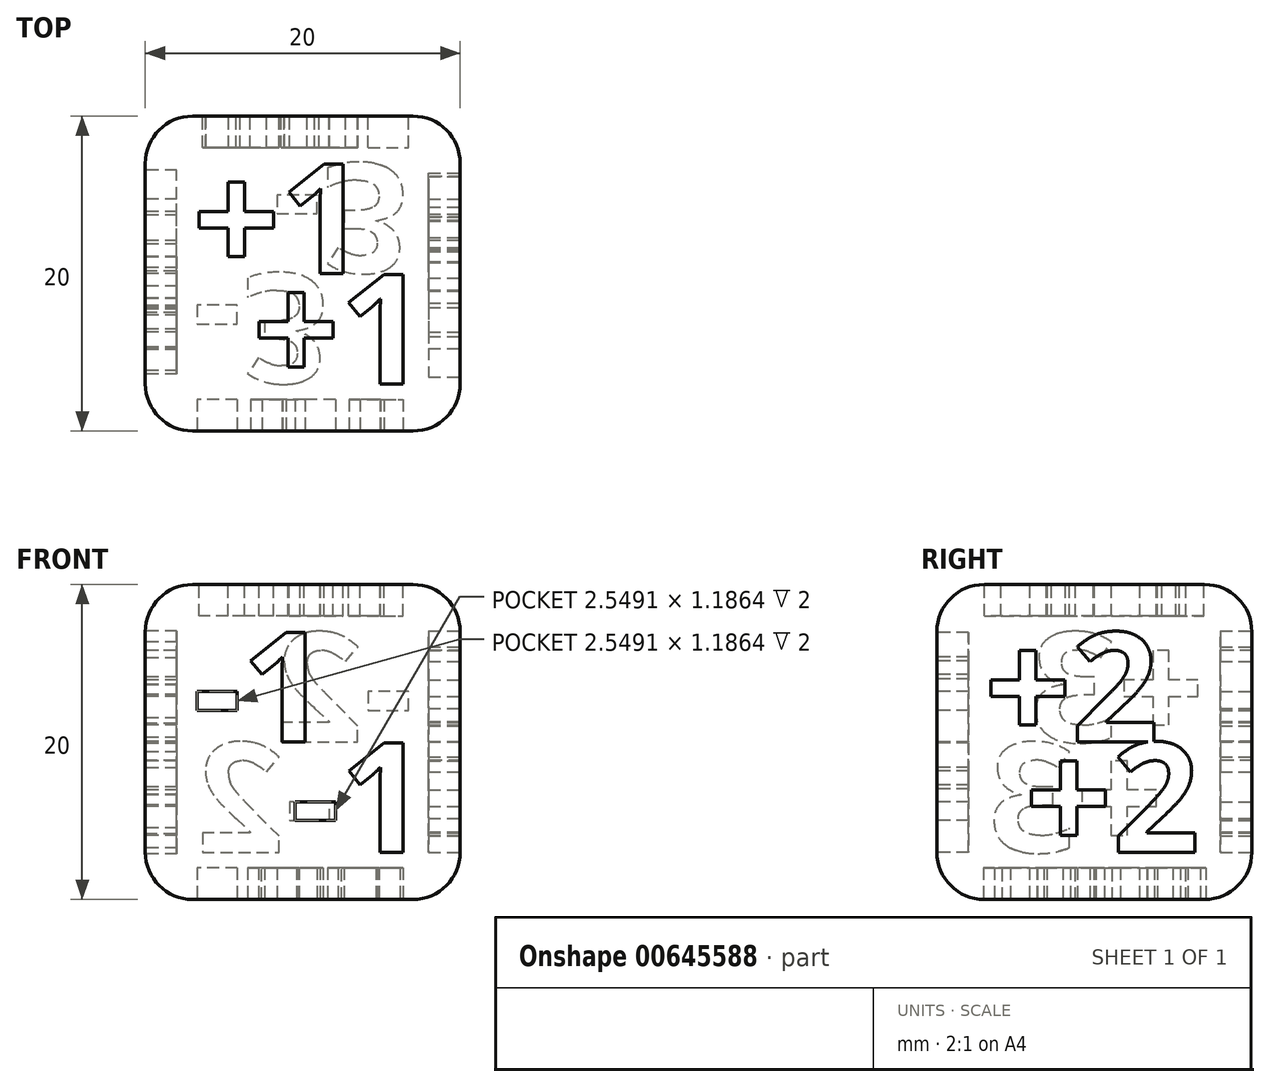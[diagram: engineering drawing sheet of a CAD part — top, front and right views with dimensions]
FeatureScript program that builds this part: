
annotation { "Feature Type Name" : "Feature", "Feature Type Description" : "" }
export const myFeature = defineFeature(function(context is Context, id is Id, definition is map)
    precondition{}
    {
        {
            var Q0;
            Q0=qCreatedBy(makeId("Top.planeOp"),FACE);
            var sketch = newSketch(context, id + "F0", { "sketchPlane" : qUnion([Q0])});
            skLineSegment(sketch, "E0.bottom", {"start": v(0, 0) * mm, "end": v(20, 0) * mm});
            skLineSegment(sketch, "E0.top", {"start": v(0, 20) * mm, "end": v(20, 20) * mm});
            skLineSegment(sketch, "E0.left", {"start": v(0, 0) * mm, "end": v(0, 20) * mm});
            skLineSegment(sketch, "E0.right", {"start": v(20, 0) * mm, "end": v(20, 20) * mm});
            skSolve(sketch);
        }
        {
            var Q0;
            Q0 = qSketchRegion(id + "F0", true);
            extrude(context, id + "F1", {"entities" : qUnion([Q0]), "depth" : 20 * mm, "offsetDistance" : 25 * mm});
        }
        {
            var Q0;
            Q0=makeQuery(id+"F1.opExtrude","CAP_EDGE",EDGE,{"disambiguationData":[OSD([sQuery(id+"F0.wireOp",EDGE,"E0.top")])],"isStart":true});
            var Q1;
            Q1=makeQuery(id+"F1.opExtrude","SWEPT_EDGE",EDGE,{"disambiguationData":[OSD([sQuery(id+"F0.wireOp",EDGE,"E0.top"),sQuery(id+"F0.wireOp",EDGE,"E0.right")])]});
            var Q2;
            Q2=makeQuery(id+"F1.opExtrude","CAP_EDGE",EDGE,{"disambiguationData":[OSD([sQuery(id+"F0.wireOp",EDGE,"E0.top")])],"isStart":false});
            var Q3;
            Q3=makeQuery(id+"F1.opExtrude","SWEPT_EDGE",EDGE,{"disambiguationData":[OSD([sQuery(id+"F0.wireOp",EDGE,"E0.top"),sQuery(id+"F0.wireOp",EDGE,"E0.left")])]});
            var Q4;
            Q4=makeQuery(id+"F1.opExtrude","CAP_EDGE",EDGE,{"disambiguationData":[OSD([sQuery(id+"F0.wireOp",EDGE,"E0.left")])],"isStart":true});
            var Q5;
            Q5=makeQuery(id+"F1.opExtrude","CAP_EDGE",EDGE,{"disambiguationData":[OSD([sQuery(id+"F0.wireOp",EDGE,"E0.left")])],"isStart":false});
            var Q6;
            Q6=makeQuery(id+"F1.opExtrude","SWEPT_EDGE",EDGE,{"disambiguationData":[OSD([sQuery(id+"F0.wireOp",EDGE,"E0.bottom"),sQuery(id+"F0.wireOp",EDGE,"E0.left")])]});
            var Q7;
            Q7=makeQuery(id+"F1.opExtrude","CAP_EDGE",EDGE,{"disambiguationData":[OSD([sQuery(id+"F0.wireOp",EDGE,"E0.right")])],"isStart":false});
            var Q8;
            Q8=makeQuery(id+"F1.opExtrude","CAP_EDGE",EDGE,{"disambiguationData":[OSD([sQuery(id+"F0.wireOp",EDGE,"E0.bottom")])],"isStart":false});
            var Q9;
            Q9=makeQuery(id+"F1.opExtrude","SWEPT_EDGE",EDGE,{"disambiguationData":[OSD([sQuery(id+"F0.wireOp",EDGE,"E0.bottom"),sQuery(id+"F0.wireOp",EDGE,"E0.right")])]});
            var Q10;
            Q10=makeQuery(id+"F1.opExtrude","CAP_EDGE",EDGE,{"disambiguationData":[OSD([sQuery(id+"F0.wireOp",EDGE,"E0.right")])],"isStart":true});
            var Q11;
            Q11=makeQuery(id+"F1.opExtrude","CAP_EDGE",EDGE,{"disambiguationData":[OSD([sQuery(id+"F0.wireOp",EDGE,"E0.bottom")])],"isStart":true});
            fillet(context, id + "F2", {"entities" : qUnion([Q0, Q1, Q2, Q3, Q4, Q5, Q6, Q7, Q8, Q9, Q10, Q11]), "radius" : 3 * mm, "tangentPropagation" : true, "allowEdgeOverflow" : false});
        }
        {
            var Q0;
            Q0=makeQuery(id+"F1.opExtrude","CAP_FACE",FACE,{"disambiguationData":[OSD([sQuery(id+"F0.wireOp",EDGE,"E0.bottom"),sQuery(id+"F0.wireOp",EDGE,"E0.top"),sQuery(id+"F0.wireOp",EDGE,"E0.left"),sQuery(id+"F0.wireOp",EDGE,"E0.right")])],"isStart":false});
            var sketch = newSketch(context, id + "F3", { "sketchPlane" : qUnion([Q0])});
            skText(sketch, "E1", { "text": "+1", "fontName": "OpenSans-Bold.ttf"});
            skText(sketch, "E2", { "text": "+1", "fontName": "OpenSans-Bold.ttf"});
            const initialGuessF3  = {"E1": [0.003, 0.01, 1, 0, 0.007], "E2": [0.0068, 0.003, 1, 0, 0.007]};
            skSetInitialGuess(sketch, initialGuessF3);
            skSolve(sketch);
        }
        {
            var Q0;
            Q0=makeQuery(id+"F1.opExtrude","SWEPT_FACE",FACE,{"disambiguationData":[OSD([sQuery(id+"F0.wireOp",EDGE,"E0.right")])]});
            var sketch = newSketch(context, id + "F4", { "sketchPlane" : qUnion([Q0])});
            skText(sketch, "E3", { "text": "+2", "fontName": "OpenSans-Bold.ttf"});
            skText(sketch, "E4", { "text": "+2", "fontName": "OpenSans-Bold.ttf"});
            const initialGuessF4  = {"E3": [0.003, 0.01, 1, 0, 0.007], "E4": [0.00558, 0.003, 1, 0, 0.007]};
            skSetInitialGuess(sketch, initialGuessF4);
            skSolve(sketch);
        }
        {
            var Q0;
            Q0=makeQuery(id+"F1.opExtrude","SWEPT_FACE",FACE,{"disambiguationData":[OSD([sQuery(id+"F0.wireOp",EDGE,"E0.left")])]});
            var sketch = newSketch(context, id + "F5", { "sketchPlane" : qUnion([Q0])});
            skText(sketch, "E5", { "text": "+3", "fontName": "OpenSans-Bold.ttf"});
            skText(sketch, "E6", { "text": "+3", "fontName": "OpenSans-Bold.ttf"});
            const initialGuessF5  = {"E5": [-0.017, 0.01, 1, 0, 0.007], "E6": [-0.01435, 0.003, 1, 0, 0.007]};
            skSetInitialGuess(sketch, initialGuessF5);
            skSolve(sketch);
        }
        {
            var Q0;
            Q0=makeQuery(id+"F1.opExtrude","SWEPT_FACE",FACE,{"disambiguationData":[OSD([sQuery(id+"F0.wireOp",EDGE,"E0.bottom")])]});
            var sketch = newSketch(context, id + "F6", { "sketchPlane" : qUnion([Q0])});
            skText(sketch, "E7", { "text": "-1", "fontName": "OpenSans-Bold.ttf"});
            skText(sketch, "E8", { "text": "-1", "fontName": "OpenSans-Bold.ttf"});
            const initialGuessF6  = {"E7": [0.003, 0.01, 1, 0, 0.007], "E8": [0.00923, 0.003, 1, 0, 0.007]};
            skSetInitialGuess(sketch, initialGuessF6);
            skSolve(sketch);
        }
        {
            var Q0;
            Q0=makeQuery(id+"F1.opExtrude","SWEPT_FACE",FACE,{"disambiguationData":[OSD([sQuery(id+"F0.wireOp",EDGE,"E0.top")])]});
            var sketch = newSketch(context, id + "F7", { "sketchPlane" : qUnion([Q0])});
            skText(sketch, "E9", { "text": "-2", "fontName": "OpenSans-Bold.ttf"});
            skText(sketch, "E10", { "text": "-2", "fontName": "OpenSans-Bold.ttf"});
            const initialGuessF7  = {"E9": [-0.017, 0.01, 1, 0, 0.007], "E10": [-0.012, 0.003, 1, 0, 0.007]};
            skSetInitialGuess(sketch, initialGuessF7);
            skSolve(sketch);
        }
        {
            var Q0;
            Q0=makeQuery(id+"F1.opExtrude","CAP_FACE",FACE,{"disambiguationData":[OSD([sQuery(id+"F0.wireOp",EDGE,"E0.bottom"),sQuery(id+"F0.wireOp",EDGE,"E0.top"),sQuery(id+"F0.wireOp",EDGE,"E0.left"),sQuery(id+"F0.wireOp",EDGE,"E0.right")])],"isStart":true});
            var sketch = newSketch(context, id + "F8", { "sketchPlane" : qUnion([Q0])});
            skText(sketch, "E11", { "text": "-3", "fontName": "OpenSans-Bold.ttf"});
            skText(sketch, "E12", { "text": "-3", "fontName": "OpenSans-Bold.ttf"});
            const initialGuessF8  = {"E11": [0.003, -0.01, 1, 0, 0.007], "E12": [0.00807, -0.017, 1, 0, 0.007]};
            skSetInitialGuess(sketch, initialGuessF8);
            skSolve(sketch);
        }
        {
            var Q0;
            Q0 = qSketchRegion(id + "F3", true);
            extrude(context, id + "F9", {"entities" : qUnion([Q0]), "operationType" : NewBodyOperationType.REMOVE, "oppositeDirection" : true, "depth" : 2 * mm, "offsetDistance" : 25 * mm});
        }
        {
            var Q0;
            Q0 = qSketchRegion(id + "F4", true);
            extrude(context, id + "F10", {"entities" : qUnion([Q0]), "operationType" : NewBodyOperationType.REMOVE, "oppositeDirection" : true, "depth" : 2 * mm, "offsetDistance" : 25 * mm});
        }
        {
            var Q0;
            Q0 = qSketchRegion(id + "F5", true);
            extrude(context, id + "F11", {"entities" : qUnion([Q0]), "operationType" : NewBodyOperationType.REMOVE, "oppositeDirection" : true, "depth" : 2 * mm, "offsetDistance" : 25 * mm});
        }
        {
            var Q0;
            Q0 = qSketchRegion(id + "F6", true);
            extrude(context, id + "F12", {"entities" : qUnion([Q0]), "operationType" : NewBodyOperationType.REMOVE, "oppositeDirection" : true, "depth" : 2 * mm, "offsetDistance" : 25 * mm});
        }
        {
            var Q0;
            Q0 = qSketchRegion(id + "F7", true);
            extrude(context, id + "F13", {"entities" : qUnion([Q0]), "operationType" : NewBodyOperationType.REMOVE, "oppositeDirection" : true, "depth" : 2 * mm, "offsetDistance" : 25 * mm});
        }
        {
            var Q0;
            Q0 = qSketchRegion(id + "F8", true);
            extrude(context, id + "F14", {"entities" : qUnion([Q0]), "operationType" : NewBodyOperationType.REMOVE, "oppositeDirection" : true, "depth" : 2 * mm, "offsetDistance" : 25 * mm});
        }
    });
